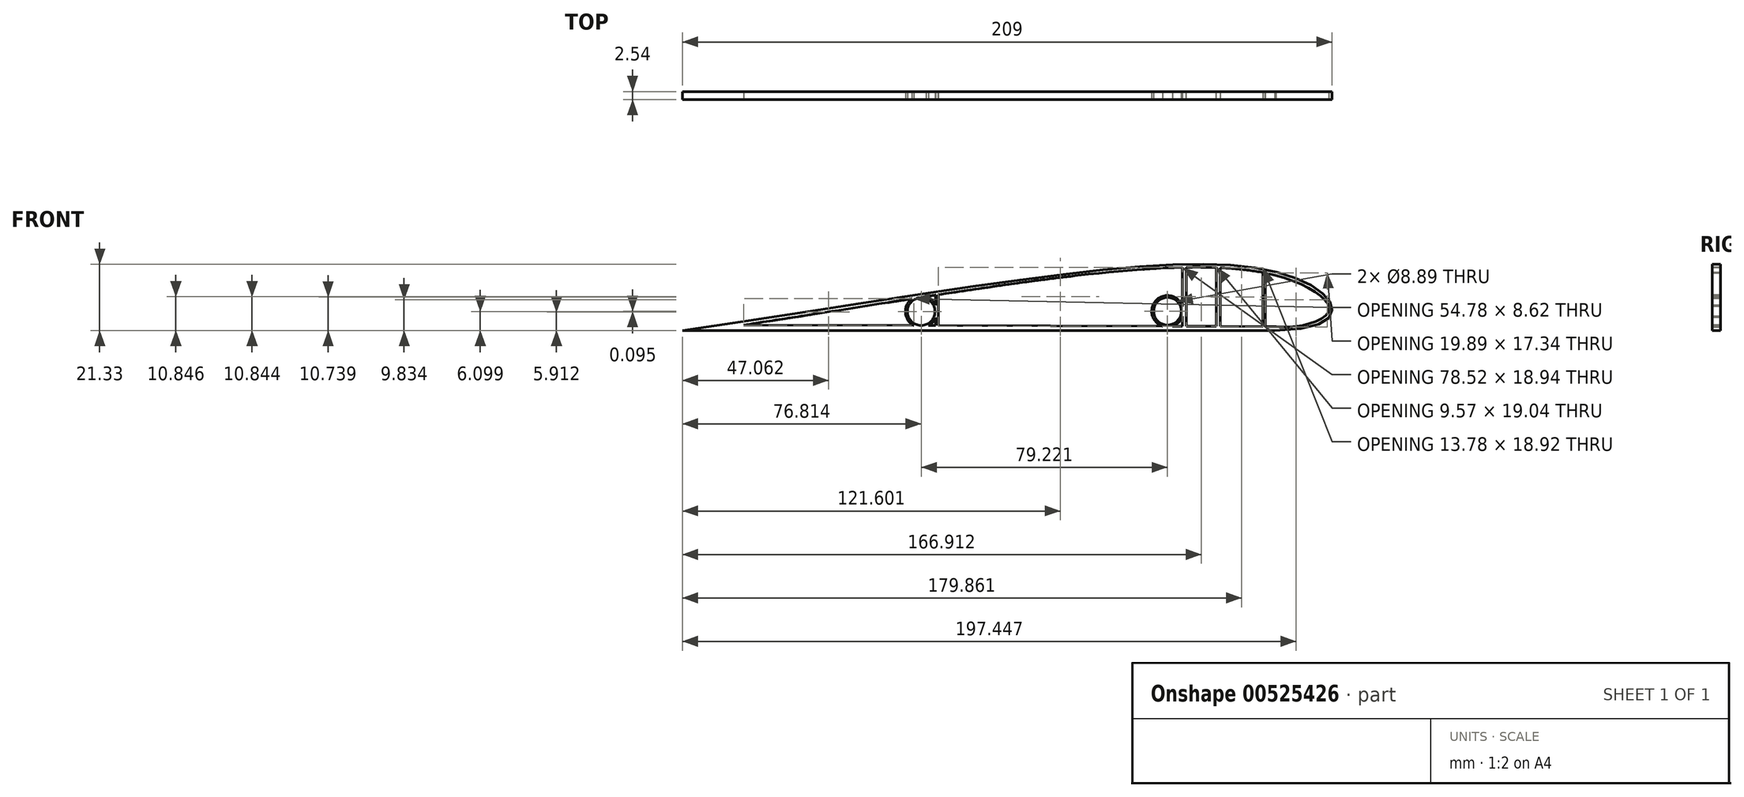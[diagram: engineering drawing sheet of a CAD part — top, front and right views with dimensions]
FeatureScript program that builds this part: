
annotation { "Feature Type Name" : "Feature", "Feature Type Description" : "" }
export const myFeature = defineFeature(function(context is Context, id is Id, definition is map)
    precondition{}
    {
        {
            var Q0;
            Q0=qCreatedBy(makeId("Front.planeOp"),FACE);
            var sketch = newSketch(context, id + "F0", { "sketchPlane" : qUnion([Q0])});
            skLineSegment(sketch, "E0", {"start": v(-106, 0) * mm, "end": v(84.5, 0) * mm});
            skFitSpline(sketch, "E1", {"points": [v(84.5, 0) * mm, v(102.86, 7.8) * mm, v(84.07, 19.05) * mm, v(-106, 0) * mm], "startDerivative": vector(228.82, 3.2) * mm, "endDerivative": vector(-504.6, -75.18) * mm});
            skSolve(sketch);
        }
        {
            var Q0;
            Q0=makeQuery(id+"F0.imprint","IMPRINT",FACE,{"disambiguationData":[TD([[makeQuery(id+"F0.imprint","IMPRINT",EDGE,{"derivedFrom":sQuery(id+"F0.wireOp",EDGE,"E0")}),1.0]])]});
            extrude(context, id + "F1", {"entities" : qUnion([Q0]), "depth" : 2.54 * mm, "offsetDistance" : 25.4 * mm});
        }
        {
            var Q0;
            Q0=makeQuery(id+"F1.opExtrude","CAP_FACE",FACE,{"disambiguationData":[OSD([sQuery(id+"F0.wireOp",EDGE,"E0"),sQuery(id+"F0.wireOp",EDGE,"E1")])],"isStart":false});
            var sketch = newSketch(context, id + "F2", { "sketchPlane" : qUnion([Q0])});
            skFitSpline(sketch, "E2", {"points": [v(84.5, 1.27) * mm, v(84.98, 1.27) * mm, v(91.61, 1.36) * mm, v(101.98, 6.55) * mm, v(91.87, 15.4) * mm, v(45.62, 19.93) * mm, v(-86.33, 1.76) * mm], "startDerivative": vector(109.48, 2.51) * mm, "endDerivative": vector(-384.03, -58.4) * mm});
            skLineSegment(sketch, "E3", {"start": v(-86.33, 1.76) * mm, "end": v(84.5, 1.27) * mm});
            skSolve(sketch);
        }
        {
            var Q0;
            Q0=makeQuery(id+"F2.imprint","IMPRINT",FACE,{"disambiguationData":[TD([[makeQuery(id+"F2.imprint","IMPRINT",EDGE,{"derivedFrom":sQuery(id+"F2.wireOp",EDGE,"E2")}),1.0]])]});
            extrude(context, id + "F3", {"entities" : qUnion([Q0]), "operationType" : NewBodyOperationType.REMOVE, "oppositeDirection" : true, "depth" : 2.54 * mm, "offsetDistance" : 25.4 * mm});
        }
        {
            var Q0;
            Q0=makeQuery(id+"F1.opExtrude","CAP_FACE",FACE,{"disambiguationData":[OSD([sQuery(id+"F0.wireOp",EDGE,"E0"),sQuery(id+"F0.wireOp",EDGE,"E1")])],"isStart":false});
            var sketch = newSketch(context, id + "F4", { "sketchPlane" : qUnion([Q0])});
            skLineSegment(sketch, "E4", {"start": v(66.98, 1.32) * mm, "end": v(65.7, 1.27) * mm});
            skLineSegment(sketch, "E5", {"start": v(65.7, 1.27) * mm, "end": v(66.98, 1.32) * mm});
            skLineSegment(sketch, "E6", {"start": v(66.97, 20.2) * mm, "end": v(65.7, 20.25) * mm});
            skLineSegment(sketch, "E7", {"start": v(54.86, 20.31) * mm, "end": v(54.86, 1.35) * mm});
            skLineSegment(sketch, "E8", {"start": v(65.7, 20.25) * mm, "end": v(65.7, 1.27) * mm});
            skLineSegment(sketch, "E9", {"start": v(66.97, 20.2) * mm, "end": v(66.98, 1.32) * mm});
            skLineSegment(sketch, "E10", {"start": v(54.86, 20.31) * mm, "end": v(56.13, 20.34) * mm});
            skLineSegment(sketch, "E11", {"start": v(56.13, 20.34) * mm, "end": v(56.13, 1.27) * mm});
            skLineSegment(sketch, "E12", {"start": v(56.13, 1.27) * mm, "end": v(54.86, 1.35) * mm});
            skSolve(sketch);
        }
        {
            var Q0;
            Q0 = qSketchRegion(id + "F4", true);
            extrude(context, id + "F5", {"entities" : qUnion([Q0]), "operationType" : NewBodyOperationType.ADD, "oppositeDirection" : true, "depth" : 2.54 * mm, "offsetDistance" : 25.4 * mm});
        }
        {
            var Q0;
            Q0=makeQuery(id+"FEWw8YBZJAngnU0_1.boolean.opBoolean","MERGE",FACE,{"derivedFrom":[makeQuery(id+"F5.boolean.opBoolean","MERGE",FACE,{"derivedFrom":[makeQuery(id+"F1.opExtrude","CAP_FACE",FACE,{"disambiguationData":[OSD([sQuery(id+"F0.wireOp",EDGE,"E0"),sQuery(id+"F0.wireOp",EDGE,"E1")])],"isStart":false}),makeQuery(id+"F5.opExtrude","CAP_FACE",FACE,{"disambiguationData":[OSD([sQuery(id+"F4.wireOp",EDGE,"7U9ZlyvD-gEdA-OMz1-83K9-VaVys2Z2WlOl"),sQuery(id+"F4.wireOp",EDGE,"esdsOQrK-YQQ0-SkDI-8f04-ihjcnlxRD0WI"),sQuery(id+"F4.wireOp",EDGE,"6hE4Fv9k-5Hfu-7tdl-H3Qt-CvJRi7VjBhap"),sQuery(id+"F4.wireOp",EDGE,"E5")])],"isStart":true}),makeQuery(id+"F5.opExtrude","CAP_FACE",FACE,{"disambiguationData":[OSD([sQuery(id+"F4.wireOp",EDGE,"UjDSfeQj-vHly-1hVj-qJBs-yy2cHhudLzjq"),sQuery(id+"F4.wireOp",EDGE,"l1BZEI7g-cfbM-4VCn-LUBx-qwcENX35hZkg"),sQuery(id+"F4.wireOp",EDGE,"29U8fcwE-jErZ-g4yI-RpAM-NayvcM1YQAya"),sQuery(id+"F4.wireOp",EDGE,"N821dQTM-D6n7-7FW6-RnI5-RDTynzZJjS1g")])],"isStart":true})]}),makeQuery(id+"FEWw8YBZJAngnU0_1.opExtrude","CAP_FACE",FACE,{"disambiguationData":[OSD([sQuery(id+"FF1hOHGw2SdKdfu_1.wireOp",EDGE,"wrmpajyc-d3W4-k6yC-MPf9-0l1dyJFj01Xq"),sQuery(id+"FF1hOHGw2SdKdfu_1.wireOp",EDGE,"QQg6mQQR-69Cg-T6Ny-Bf4n-1nVzowcEqM3W"),sQuery(id+"FF1hOHGw2SdKdfu_1.wireOp",EDGE,"maxqLWiG-y28s-eWaT-mYOg-P5XK7B49JnDO"),sQuery(id+"FF1hOHGw2SdKdfu_1.wireOp",EDGE,"nFGz1nlY-YASl-u5fq-tUg5-CBekJo7RrcsD")])],"isStart":true}),makeQuery(id+"FEWw8YBZJAngnU0_1.opExtrude","CAP_FACE",FACE,{"disambiguationData":[OSD([sQuery(id+"FF1hOHGw2SdKdfu_1.wireOp",EDGE,"SCzdr7Jd-3WiP-F2gb-xvBj-j2M8Qtpxfrae"),sQuery(id+"FF1hOHGw2SdKdfu_1.wireOp",EDGE,"tnrZBpPv-Josb-Q2wh-fvVj-vxKkK1rRAKdB"),sQuery(id+"FF1hOHGw2SdKdfu_1.wireOp",EDGE,"a8rwBpXL-h8cV-EfJZ-2J42-Fzwst47fqpbR"),sQuery(id+"FF1hOHGw2SdKdfu_1.wireOp",EDGE,"9paBAGkQ-BTRR-jBYo-kABq-VvwknmRGVJgN")])],"isStart":true})]});
            var sketch = newSketch(context, id + "F6", { "sketchPlane" : qUnion([Q0])});
            skCircle(sketch, "E13", {"center": v(50.04, 6.2) * mm, "radius": 5.08 * mm});
            skCircle(sketch, "E14", {"center": v(50.04, 6.2) * mm, "radius": 4.45 * mm});
            skSolve(sketch);
        }
        {
            var Q0;
            Q0 = qSketchRegion(id + "F6", true);
            extrude(context, id + "F7", {"entities" : qUnion([Q0]), "operationType" : NewBodyOperationType.ADD, "oppositeDirection" : true, "depth" : 2.54 * mm, "offsetDistance" : 25.4 * mm});
        }
        {
            var Q0;
            Q0=makeQuery(id+"F7.boolean.opBoolean","MERGE",FACE,{"derivedFrom":[makeQuery(id+"F5.boolean.opBoolean","MERGE",FACE,{"derivedFrom":[makeQuery(id+"F1.opExtrude","CAP_FACE",FACE,{"disambiguationData":[OSD([sQuery(id+"F0.wireOp",EDGE,"E0"),sQuery(id+"F0.wireOp",EDGE,"E1")])],"isStart":false}),makeQuery(id+"F5.opExtrude","CAP_FACE",FACE,{"disambiguationData":[OSD([sQuery(id+"F4.wireOp",EDGE,"N821dQTM-D6n7-7FW6-RnI5-RDTynzZJjS1g"),sQuery(id+"F4.wireOp",EDGE,"5kyGtuvI-sTVK-6TOU-M405-Wd376OI7nIWL"),sQuery(id+"F4.wireOp",EDGE,"LbH4qvnV-3cJ3-Oz80-bYPv-3kEOOjAEs28X"),sQuery(id+"F4.wireOp",EDGE,"G1ZI1qNu-2QF1-pMsK-TtSh-2s5Wpc0kY9jK")])],"isStart":true}),makeQuery(id+"F5.opExtrude","CAP_FACE",FACE,{"disambiguationData":[OSD([sQuery(id+"F4.wireOp",EDGE,"E5"),sQuery(id+"F4.wireOp",EDGE,"KBOGrDtw-cqld-99i6-KTJl-WohceKqummJH"),sQuery(id+"F4.wireOp",EDGE,"E6"),sQuery(id+"F4.wireOp",EDGE,"IN7H59ia-YICV-ZNQJ-EpXy-WgWZX2zn3Wo8")])],"isStart":true}),makeQuery(id+"F5.opExtrude","CAP_FACE",FACE,{"disambiguationData":[OSD([sQuery(id+"F4.wireOp",EDGE,"wnajp0au-dybZ-Mwin-WfjU-281j0zXTk0Ag"),sQuery(id+"F4.wireOp",EDGE,"SvxMS3Xs-76js-ricT-y9RV-ihEYhjUvyLpx"),sQuery(id+"F4.wireOp",EDGE,"oZoKInsc-qbg1-t7h1-6W5F-8BZYpw6vMWzY"),sQuery(id+"F4.wireOp",EDGE,"imItZmDT-U31D-K2z6-48O4-8SzDzLfAPiHQ")])],"isStart":true})]}),makeQuery(id+"F7.opExtrude","CAP_FACE",FACE,{"disambiguationData":[OSD([sQuery(id+"F6.wireOp",EDGE,"E13"),sQuery(id+"F6.wireOp",EDGE,"E14")])],"isStart":true})]});
            var sketch = newSketch(context, id + "F8", { "sketchPlane" : qUnion([Q0])});
            skLineSegment(sketch, "E15", {"start": v(-24.5, 11.4) * mm, "end": v(-23.66, 11.53) * mm});
            skLineSegment(sketch, "E16", {"start": v(-23.66, 11.53) * mm, "end": v(-23.66, 1.58) * mm});
            skLineSegment(sketch, "E17", {"start": v(-24.5, 11.4) * mm, "end": v(-24.5, 1.58) * mm});
            skLineSegment(sketch, "E18", {"start": v(-24.5, 1.58) * mm, "end": v(-23.66, 1.58) * mm});
            skSolve(sketch);
        }
        {
            var Q0;
            Q0 = qSketchRegion(id + "F8", true);
            extrude(context, id + "F9", {"entities" : qUnion([Q0]), "operationType" : NewBodyOperationType.ADD, "oppositeDirection" : true, "depth" : 2.54 * mm, "offsetDistance" : 25.4 * mm});
        }
        {
            var Q0;
            Q0=makeQuery(id+"F9.boolean.opBoolean","MERGE",FACE,{"derivedFrom":[makeQuery(id+"F7.boolean.opBoolean","MERGE",FACE,{"derivedFrom":[makeQuery(id+"F5.boolean.opBoolean","MERGE",FACE,{"derivedFrom":[makeQuery(id+"F1.opExtrude","CAP_FACE",FACE,{"disambiguationData":[OSD([sQuery(id+"F0.wireOp",EDGE,"E0"),sQuery(id+"F0.wireOp",EDGE,"E1")])],"isStart":false}),makeQuery(id+"F5.opExtrude","CAP_FACE",FACE,{"disambiguationData":[OSD([sQuery(id+"F4.wireOp",EDGE,"E5"),sQuery(id+"F4.wireOp",EDGE,"E6"),sQuery(id+"F4.wireOp",EDGE,"E8"),sQuery(id+"F4.wireOp",EDGE,"E9")])],"isStart":true}),makeQuery(id+"F5.opExtrude","CAP_FACE",FACE,{"disambiguationData":[OSD([sQuery(id+"F4.wireOp",EDGE,"E7"),sQuery(id+"F4.wireOp",EDGE,"E10"),sQuery(id+"F4.wireOp",EDGE,"E11"),sQuery(id+"F4.wireOp",EDGE,"E12")])],"isStart":true})]}),makeQuery(id+"F7.opExtrude","CAP_FACE",FACE,{"disambiguationData":[OSD([sQuery(id+"F6.wireOp",EDGE,"E13"),sQuery(id+"F6.wireOp",EDGE,"E14")])],"isStart":true})]}),makeQuery(id+"F9.opExtrude","CAP_FACE",FACE,{"disambiguationData":[OSD([sQuery(id+"F8.wireOp",EDGE,"E15"),sQuery(id+"F8.wireOp",EDGE,"E16"),sQuery(id+"F8.wireOp",EDGE,"E17"),sQuery(id+"F8.wireOp",EDGE,"E18")])],"isStart":true})]});
            var sketch = newSketch(context, id + "F10", { "sketchPlane" : qUnion([Q0])});
            skLineSegment(sketch, "E19", {"start": v(80.75, 18.65) * mm, "end": v(80.75, 1.28) * mm});
            skLineSegment(sketch, "E20", {"start": v(80.75, 1.28) * mm, "end": v(81.5, 1.28) * mm});
            skLineSegment(sketch, "E21", {"start": v(81.5, 1.28) * mm, "end": v(81.5, 18.5) * mm});
            skLineSegment(sketch, "E22", {"start": v(81.5, 18.5) * mm, "end": v(80.75, 18.65) * mm});
            skSolve(sketch);
        }
        {
            var Q0;
            Q0 = qSketchRegion(id + "F10", true);
            extrude(context, id + "F11", {"entities" : qUnion([Q0]), "operationType" : NewBodyOperationType.ADD, "oppositeDirection" : true, "depth" : 2.54 * mm, "offsetDistance" : 25.4 * mm});
        }
        {
            var Q0;
            Q0=makeQuery(id+"F11.boolean.opBoolean","MERGE",FACE,{"derivedFrom":[makeQuery(id+"F9.boolean.opBoolean","MERGE",FACE,{"derivedFrom":[makeQuery(id+"F7.boolean.opBoolean","MERGE",FACE,{"derivedFrom":[makeQuery(id+"F5.boolean.opBoolean","MERGE",FACE,{"derivedFrom":[makeQuery(id+"F1.opExtrude","CAP_FACE",FACE,{"disambiguationData":[OSD([sQuery(id+"F0.wireOp",EDGE,"E0"),sQuery(id+"F0.wireOp",EDGE,"E1")])],"isStart":false}),makeQuery(id+"F5.opExtrude","CAP_FACE",FACE,{"disambiguationData":[OSD([sQuery(id+"F4.wireOp",EDGE,"E5"),sQuery(id+"F4.wireOp",EDGE,"E6"),sQuery(id+"F4.wireOp",EDGE,"E8"),sQuery(id+"F4.wireOp",EDGE,"E9")])],"isStart":true}),makeQuery(id+"F5.opExtrude","CAP_FACE",FACE,{"disambiguationData":[OSD([sQuery(id+"F4.wireOp",EDGE,"E7"),sQuery(id+"F4.wireOp",EDGE,"E10"),sQuery(id+"F4.wireOp",EDGE,"E11"),sQuery(id+"F4.wireOp",EDGE,"E12")])],"isStart":true})]}),makeQuery(id+"F7.opExtrude","CAP_FACE",FACE,{"disambiguationData":[OSD([sQuery(id+"F6.wireOp",EDGE,"E13"),sQuery(id+"F6.wireOp",EDGE,"E14")])],"isStart":true})]}),makeQuery(id+"F9.opExtrude","CAP_FACE",FACE,{"disambiguationData":[OSD([sQuery(id+"F8.wireOp",EDGE,"E15"),sQuery(id+"F8.wireOp",EDGE,"E16"),sQuery(id+"F8.wireOp",EDGE,"E17"),sQuery(id+"F8.wireOp",EDGE,"E18")])],"isStart":true})]}),makeQuery(id+"F11.opExtrude","CAP_FACE",FACE,{"disambiguationData":[OSD([sQuery(id+"F10.wireOp",EDGE,"E19"),sQuery(id+"F10.wireOp",EDGE,"E20"),sQuery(id+"F10.wireOp",EDGE,"E21"),sQuery(id+"F10.wireOp",EDGE,"E22")])],"isStart":true})]});
            var sketch = newSketch(context, id + "F12", { "sketchPlane" : qUnion([Q0])});
            skCircle(sketch, "E23", {"center": v(-29.19, 6.1) * mm, "radius": 5.08 * mm});
            skCircle(sketch, "E24", {"center": v(-29.19, 6.1) * mm, "radius": 4.45 * mm});
            skSolve(sketch);
        }
        {
            var Q0;
            Q0 = qSketchRegion(id + "F12", true);
            extrude(context, id + "F13", {"entities" : qUnion([Q0]), "operationType" : NewBodyOperationType.ADD, "oppositeDirection" : true, "depth" : 2.54 * mm, "offsetDistance" : 25.4 * mm});
        }
    });
